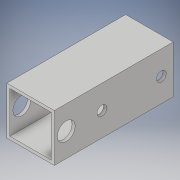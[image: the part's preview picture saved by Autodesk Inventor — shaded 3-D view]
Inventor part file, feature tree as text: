
AUTODESK INVENTOR PART (.ipt)
format: ipt  version: 2018 (Build 220112000, 112)  size: 122,880 bytes
history: native  units: in
note: dims shown in document units (in); Inventor stores cm internally (conversion verified against a paired STEP export)
features: extrude x2, sketch x2
ambient origin geometry x8: Origin, YZ Plane, XZ Plane, XY Plane, X Axis, Y Axis, Z Axis, Center Point
bodies: Solid1 (feature_tree)
feature tree (4):
  extrude  "Extrusion1"  Depth=1.0in
  extrude  "Extrusion2"  Depth=2.5in TaperAngle=0.0deg
  sketch  "Sketch1"  dims[d0=1.0in d1=1.0in]
  sketch  "Sketch2"  dims[d2=0.065in d3=2.5in d4=0.0in d5=0.375in d6=0.25in d7=0.2031in d8=0.2031in d9=0.75in d10=0.25in d11=0.5in d12=0.5in d13=0.5in d14=2.0in d15=0.0in]
